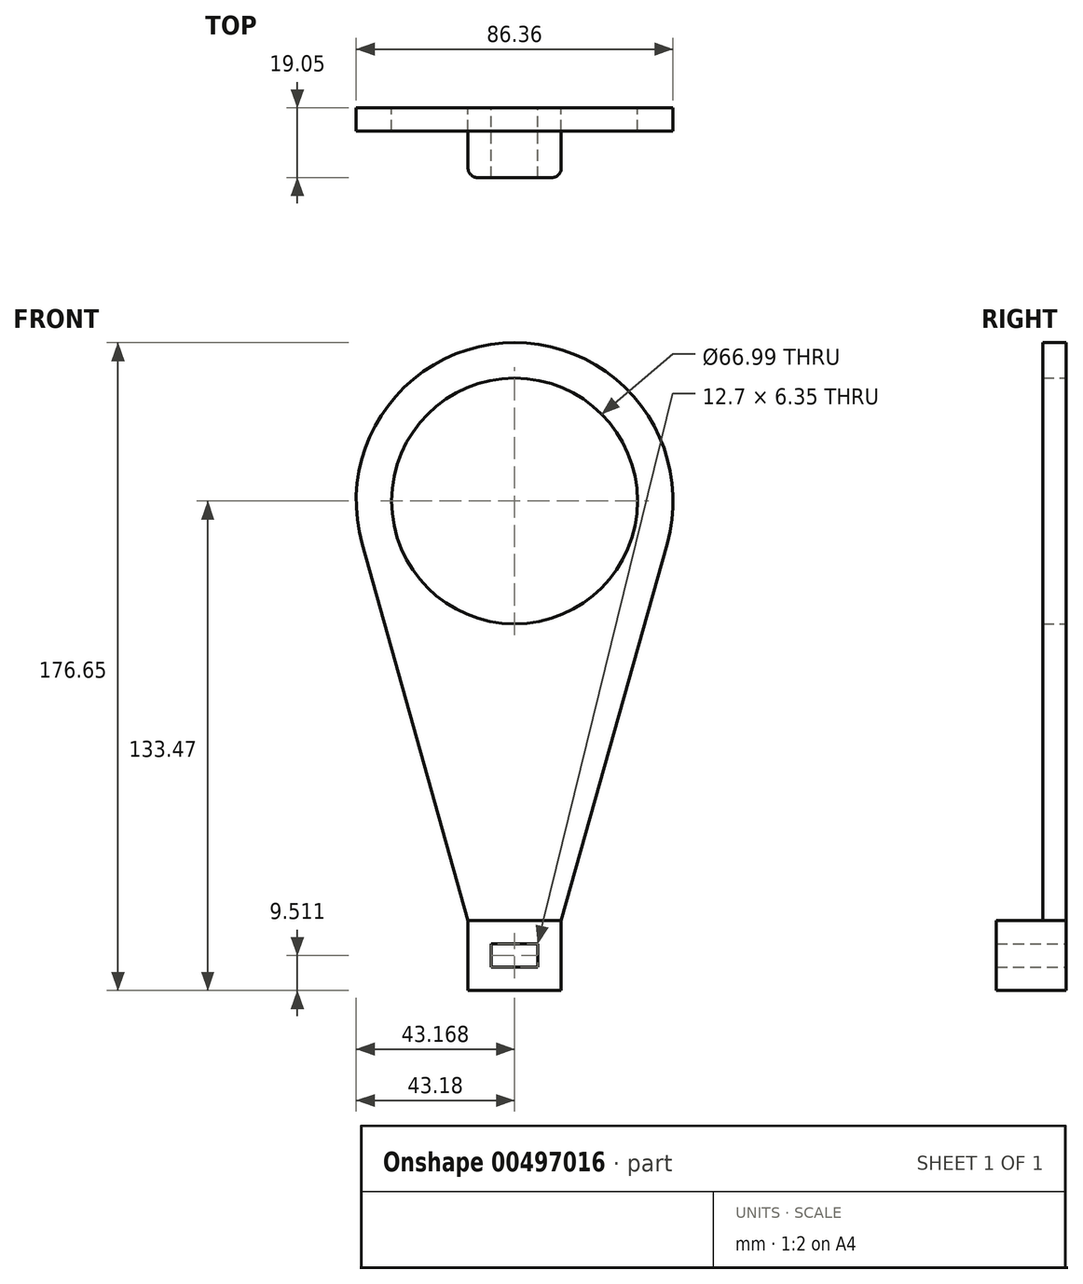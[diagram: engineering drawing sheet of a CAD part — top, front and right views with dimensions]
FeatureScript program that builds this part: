
annotation { "Feature Type Name" : "Feature", "Feature Type Description" : "" }
export const myFeature = defineFeature(function(context is Context, id is Id, definition is map)
    precondition{}
    {
        {
            var Q0;
            Q0=qCreatedBy(makeId("Front.planeOp"),FACE);
            var sketch = newSketch(context, id + "F0", { "sketchPlane" : qUnion([Q0])});
            skCircle(sketch, "E0", {"center": v(0, 0) * mm, "radius": 33.5 * mm});
            skCircle(sketch, "E1", {"center": v(0, 0) * mm, "radius": 43.18 * mm});
            skLineSegment(sketch, "E2.right", {"start": v(6.34, -127.13) * mm, "end": v(6.34, -120.78) * mm});
            skLineSegment(sketch, "E3.right", {"start": v(-6.36, -127.13) * mm, "end": v(-6.36, -120.78) * mm});
            skLineSegment(sketch, "E4", {"start": v(-6.36, -127.13) * mm, "end": v(6.34, -127.13) * mm});
            skLineSegment(sketch, "E5", {"start": v(-12.7, -133.47) * mm, "end": v(12.7, -133.47) * mm});
            skLineSegment(sketch, "E6", {"start": v(-12.7, -114.46) * mm, "end": v(12.7, -114.42) * mm});
            skLineSegment(sketch, "E7", {"start": v(-6.36, -120.78) * mm, "end": v(6.34, -120.78) * mm});
            skLineSegment(sketch, "E8", {"start": v(-12.7, -114.46) * mm, "end": v(-41.57, -11.68) * mm});
            skLineSegment(sketch, "E9", {"start": v(12.7, -114.42) * mm, "end": v(41.57, -11.68) * mm});
            skLineSegment(sketch, "E10", {"start": v(-12.7, -114.46) * mm, "end": v(-12.7, -133.47) * mm});
            skLineSegment(sketch, "E11", {"start": v(12.7, -114.42) * mm, "end": v(12.7, -133.47) * mm});
            skSolve(sketch);
        }
        {
            var Q0;
            Q0=qSketchRegion(id+"F0",true);
            extrude(context, id + "F1", {"entities" : qUnion([Q0]), "depth" : 6.35 * mm});
        }
        {
            var Q0;
            Q0=makeQuery(id+"F0.imprint","IMPRINT",FACE,{"disambiguationData":[TD([[makeQuery(id+"F0.imprint","IMPRINT",EDGE,{"derivedFrom":sQuery(id+"F0.wireOp",EDGE,"E2.right")}),-1.0]])]});
            extrude(context, id + "F2", {"entities" : qUnion([Q0]), "operationType" : NewBodyOperationType.ADD, "depth" : 19.05 * mm});
        }
        {
            var Q0;
            Q0=makeQuery(id+"F2.opExtrude","CAP_EDGE",EDGE,{"disambiguationData":[OSD([sQuery(id+"F0.wireOp",EDGE,"E10")])],"isStart":false});
            var Q1;
            Q1=makeQuery(id+"F2.opExtrude","CAP_EDGE",EDGE,{"disambiguationData":[OSD([sQuery(id+"F0.wireOp",EDGE,"E11")])],"isStart":false});
            fillet(context, id + "F3", {"entities" : qUnion([Q0, Q1]), "radius" : 2.54 * mm, "tangentPropagation" : true, "allowEdgeOverflow" : false});
        }
    });
